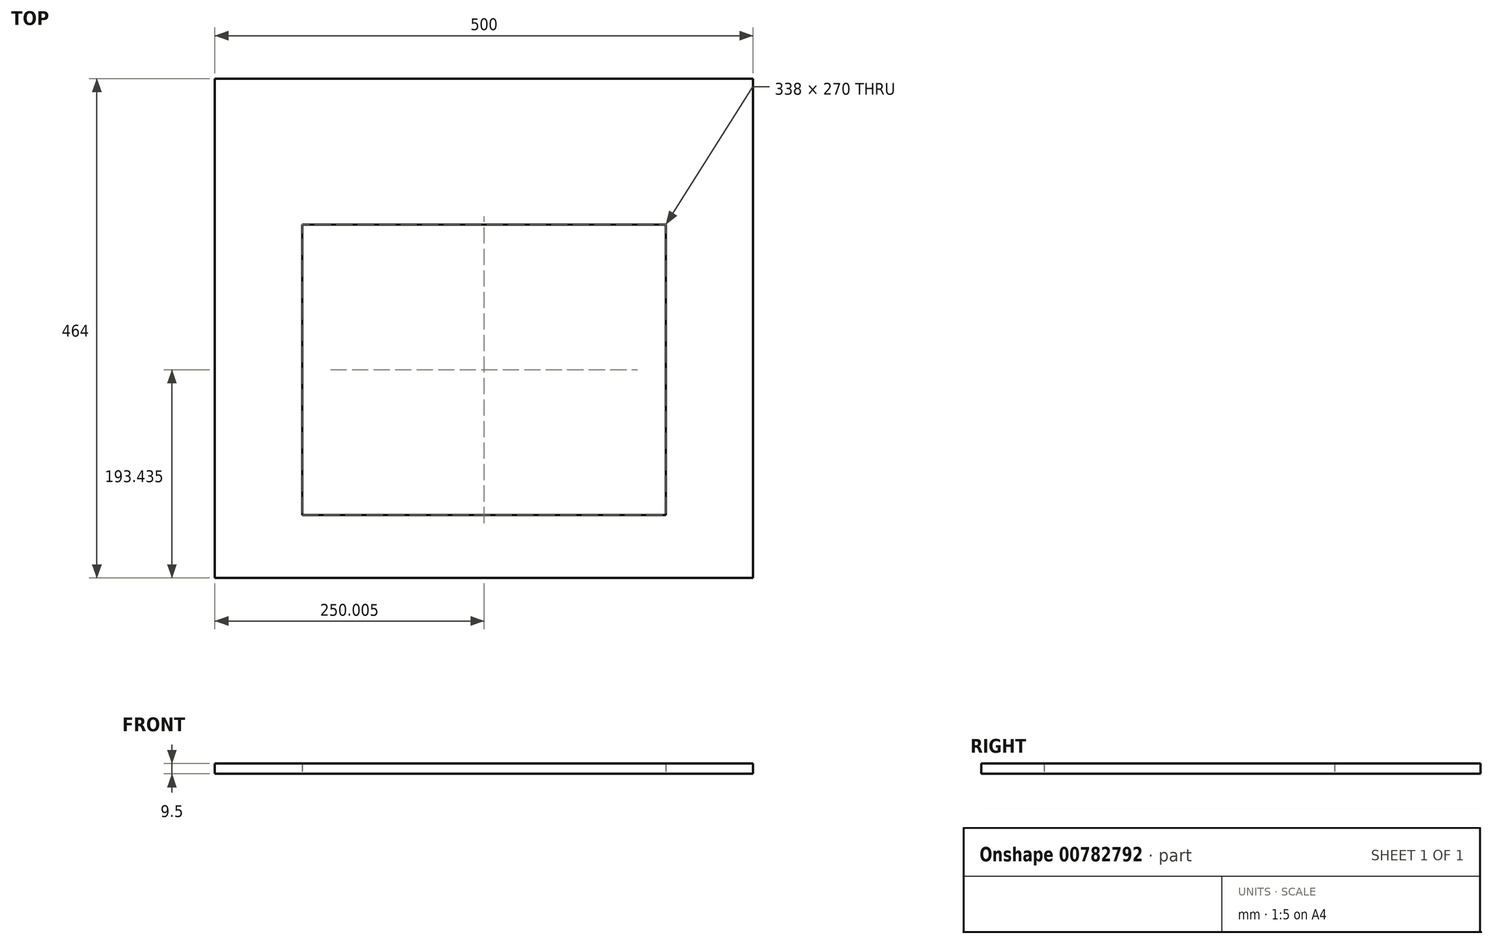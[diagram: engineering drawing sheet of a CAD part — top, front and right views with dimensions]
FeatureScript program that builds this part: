
annotation { "Feature Type Name" : "Feature", "Feature Type Description" : "" }
export const myFeature = defineFeature(function(context is Context, id is Id, definition is map)
    precondition{}
    {
        {
            var Q0;
            Q0=qCreatedBy(makeId("Top.planeOp"),FACE);
            var sketch = newSketch(context, id + "F0", { "sketchPlane" : qUnion([Q0])});
            skLineSegment(sketch, "E0", {"start": v(-50.92, 447.95) * mm, "end": v(-50.92, -16.05) * mm});
            skLineSegment(sketch, "E1", {"start": v(449.08, -16.05) * mm, "end": v(449.08, 447.95) * mm});
            skLineSegment(sketch, "E2", {"start": v(449.08, 447.95) * mm, "end": v(-50.92, 447.95) * mm});
            skLineSegment(sketch, "E3", {"start": v(-50.92, -16.05) * mm, "end": v(449.08, -16.05) * mm});
            skLineSegment(sketch, "E4", {"start": v(199.08, 312.39) * mm, "end": v(368.08, 312.39) * mm});
            skLineSegment(sketch, "E5", {"start": v(368.08, 312.39) * mm, "end": v(368.08, 42.39) * mm});
            skLineSegment(sketch, "E6", {"start": v(368.08, 42.39) * mm, "end": v(30.08, 42.39) * mm});
            skLineSegment(sketch, "E7", {"start": v(30.08, 42.39) * mm, "end": v(30.08, 312.39) * mm});
            skLineSegment(sketch, "E8", {"start": v(30.08, 312.39) * mm, "end": v(199.08, 312.39) * mm});
            skSolve(sketch);
        }
        {
            var Q0;
            Q0=makeQuery(id+"F0.imprint","IMPRINT",FACE,{"disambiguationData":[TD([[makeQuery(id+"F0.imprint","IMPRINT",EDGE,{"derivedFrom":sQuery(id+"F0.wireOp",EDGE,"E0")}),1.0]])]});
            extrude(context, id + "F1", {"entities" : qUnion([Q0]), "depth" : 9.5 * mm, "offsetDistance" : 25 * mm});
        }
    });
